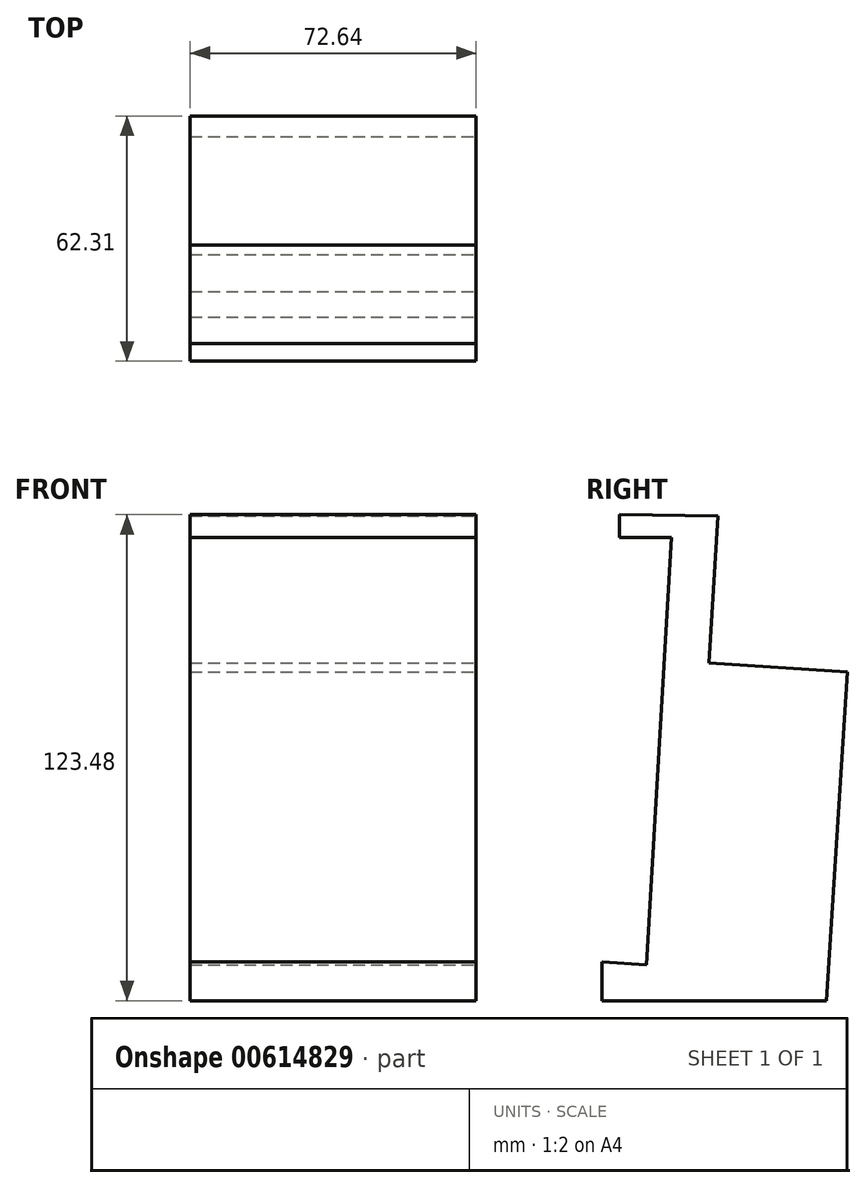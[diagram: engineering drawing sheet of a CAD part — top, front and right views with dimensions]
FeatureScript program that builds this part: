
annotation { "Feature Type Name" : "Feature", "Feature Type Description" : "" }
export const myFeature = defineFeature(function(context is Context, id is Id, definition is map)
    precondition{}
    {
        {
            var Q0;
            Q0=qCreatedBy(makeId("Right.planeOp"),FACE);
            var sketch = newSketch(context, id + "F0", { "sketchPlane" : qUnion([Q0])});
            skLineSegment(sketch, "E0", {"start": v(-52.6, 57.85) * mm, "end": v(-52.6, 52.1) * mm});
            skLineSegment(sketch, "E1", {"start": v(-52.6, 52.1) * mm, "end": v(-39.41, 52.1) * mm});
            skLineSegment(sketch, "E2", {"start": v(-39.41, 52.1) * mm, "end": v(-45.84, -56.5) * mm});
            skLineSegment(sketch, "E3", {"start": v(-45.84, -56.5) * mm, "end": v(-57.07, -55.83) * mm});
            skLineSegment(sketch, "E4", {"start": v(-57.07, -55.83) * mm, "end": v(-57.07, -65.63) * mm});
            skLineSegment(sketch, "E5", {"start": v(-57.07, -65.63) * mm, "end": v(0, -65.63) * mm});
            skLineSegment(sketch, "E6", {"start": v(0, -65.63) * mm, "end": v(5.24, 17.93) * mm});
            skLineSegment(sketch, "E7", {"start": v(5.24, 17.93) * mm, "end": v(-29.95, 20.14) * mm});
            skLineSegment(sketch, "E8", {"start": v(-29.95, 20.14) * mm, "end": v(-27.6, 57.51) * mm});
            skLineSegment(sketch, "E9", {"start": v(-27.6, 57.51) * mm, "end": v(-52.6, 57.85) * mm});
            skSolve(sketch);
        }
        {
            var Q0;
            Q0=makeQuery(id+"F0.imprint","IMPRINT",FACE,{"disambiguationData":[TD([[makeQuery(id+"F0.imprint","IMPRINT",EDGE,{"derivedFrom":sQuery(id+"F0.wireOp",EDGE,"E0")}),1.0]])]});
            extrude(context, id + "F1", {"entities" : qUnion([Q0]), "oppositeDirection" : true, "depth" : 36.32 * mm, "offsetDistance" : 25.4 * mm, "hasSecondDirection" : true, "secondDirectionOppositeDirection" : false, "secondDirectionDepth" : 36.32 * mm});
        }
        {
            var Q0;
            Q0=makeQuery(id+"F1.opExtrude","SWEPT_FACE",FACE,{"disambiguationData":[OSD([sQuery(id+"F0.wireOp",EDGE,"E7")])]});
            extrude(context, id + "F2", {"entities" : qUnion([Q0]), "operationType" : NewBodyOperationType.ADD, "oppositeDirection" : true, "depth" : 67.82 * mm, "offsetDistance" : 25.4 * mm});
        }
    });
